# Revit family: 337621xx0--Semi-pedestal-Hall-337621xx0
name_source: partatom
category: Plumbing Fixtures
units: mm (PartAtom-declared; Revit-internal decimal feet)

## family parameters
Always vertical = Yes
Cut with Voids When Loaded = No
Host = Wall
OmniClass Number = 23.45.05.14.11
OmniClass Title = Sanitary Washing Unit Components
Part Type = Normal
Room Calculation Point = No
Round Connector Dimension = Use Diameter
Shared = No

## types (4) — shared parameters
BIMobject category = Basins
Date of publishing = 2012-06-01
Depth = 230.00
Description = Vitreous china semipedestal for basin
Height = 360 mm  [stored 1.1811 ft]
IFC Classification = Furnishing Element
Length = 230 mm  [stored 0.754593 ft]
Manufacturer URL = http://www.roca.com
Manufacturer name = Roca
Model = 337621..0
NBS Reference Code = 35-65-70-94
NBS Reference Description = Wash Basin Systems
Nominal height = 360.00
Nominal width = 360.00
Product Guid = a2630a00-3f5d-4590-b8b5-2e4c965a52d5
Product data url = http://roca.bimobject.com
Product family = Hall
Product group = COVERS AND DIVISIONS
QR code = https://www.roca.com
Technical description = http://www.roca.com
UNSPSC Code = 301815
URL = http://www.roca.com
Uniclass 1.4 Code = L7212
Uniclass 1.4 Description = Washbasins
Uniclass 2.0 Code = SS-35-65-70-94
Uniclass 2.0 Description = Wash Basin Systems
Weight Net (Kg) = 0
Width = 360 mm  [stored 1.1811 ft]
zero-valued in all types: Edition number

## per-type parameters (varying)
| type | Imported Category Visibility 01 | Imported Category Visibility 02 | Imported Category Visibility 03 | Imported Category Visibility 04 | Primary Material | Product SKU |
| 337621000 White | Yes | No | No | No | White - Hall - Roca | A337621000 |
| 337621170 Pergamon | No | Yes | No | No | Pergamon - Hall - Roca | A337621170 |
| 337621910 Edelweiss | No | No | Yes | No | Edelweiss - Hall - Roca | A337621910 |
| 337621920 Graphit | No | No | No | Yes | Graphit - Hall - Roca | A337621920 |

note: [stored X ft] marks values corroborated as IEEE doubles in the binary element streams (Revit-internal decimal feet)

## geometry (parser evidence)
native form markers: Blend x4, Sweep x6
no freeform markers — native parametric forms only
